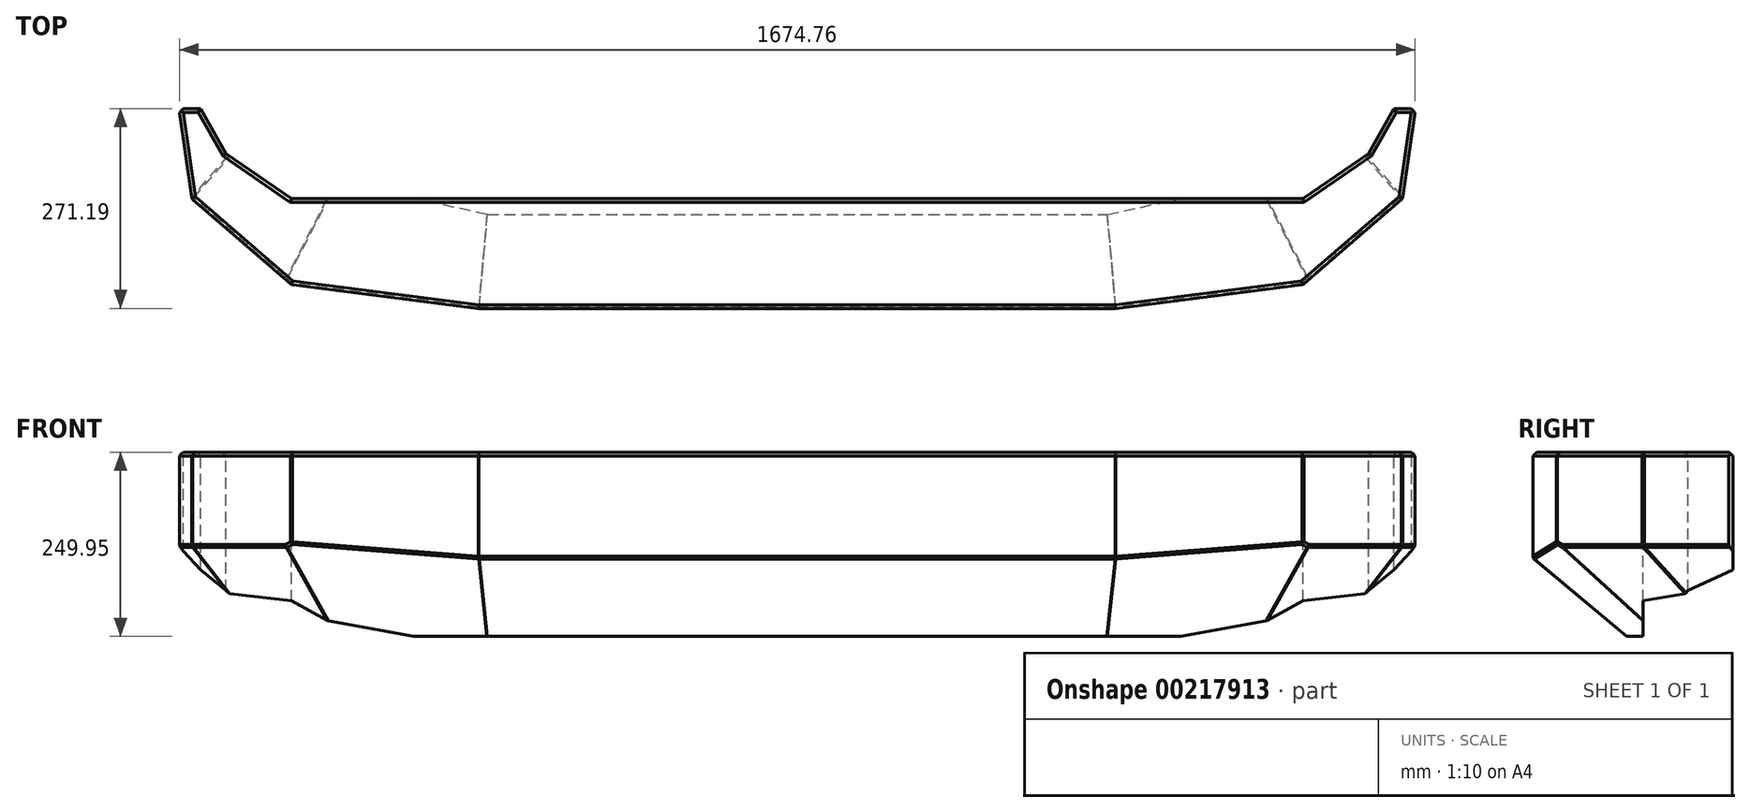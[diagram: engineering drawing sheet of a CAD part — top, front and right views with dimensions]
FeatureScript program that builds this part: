
annotation { "Feature Type Name" : "Feature", "Feature Type Description" : "" }
export const myFeature = defineFeature(function(context is Context, id is Id, definition is map)
    precondition{}
    {
        {
            var Q0;
            Q0=qCreatedBy(makeId("Top.planeOp"),FACE);
            var sketch = newSketch(context, id + "F0", { "sketchPlane" : qUnion([Q0])});
            skLineSegment(sketch, "E0", {"start": v(0, 0) * mm, "end": v(0, 79.38) * mm});
            skLineSegment(sketch, "E1", {"start": v(0, 0) * mm, "end": v(685.8, 0) * mm});
            skLineSegment(sketch, "E2", {"start": v(685.8, 0) * mm, "end": v(774.89, 60.96) * mm});
            skLineSegment(sketch, "E3", {"start": v(774.89, 60.96) * mm, "end": v(809, 121.92) * mm});
            skLineSegment(sketch, "E4", {"start": v(809, 121.92) * mm, "end": v(838.2, 121.92) * mm});
            skLineSegment(sketch, "E5", {"start": v(838.2, 121.92) * mm, "end": v(820.92, 0) * mm});
            skLineSegment(sketch, "E6", {"start": v(820.92, 0) * mm, "end": v(685.8, -117.08) * mm});
            skLineSegment(sketch, "E7", {"start": v(685.8, -117.08) * mm, "end": v(431.8, -149.27) * mm});
            skLineSegment(sketch, "E8", {"start": v(431.8, -149.27) * mm, "end": v(0, -149.27) * mm});
            skPoint(sketch, "E9", {"position": v(829.56, 60.96) * mm});
            skLineSegment(sketch, "E10.MirrorCS", {"start": v(0, 0) * mm, "end": v(-685.8, 0) * mm});
            skLineSegment(sketch, "E11.MirrorCS", {"start": v(-431.8, -149.27) * mm, "end": v(0, -149.27) * mm});
            skLineSegment(sketch, "E12.MirrorCS", {"start": v(-685.8, -117.08) * mm, "end": v(-431.8, -149.27) * mm});
            skLineSegment(sketch, "E13.MirrorCS", {"start": v(-820.92, 0) * mm, "end": v(-685.8, -117.08) * mm});
            skPoint(sketch, "E14.MirrorP", {"position": v(-829.56, 60.96) * mm});
            skLineSegment(sketch, "E15.MirrorCS", {"start": v(-838.2, 121.92) * mm, "end": v(-820.92, 0) * mm});
            skLineSegment(sketch, "E16.MirrorCS", {"start": v(-809, 121.92) * mm, "end": v(-838.2, 121.92) * mm});
            skLineSegment(sketch, "E17.MirrorCS", {"start": v(-774.89, 60.96) * mm, "end": v(-809, 121.92) * mm});
            skLineSegment(sketch, "E18.MirrorCS", {"start": v(-685.8, 0) * mm, "end": v(-774.89, 60.96) * mm});
            skSolve(sketch);
        }
        {
            var Q0;
            Q0 = qSketchRegion(id + "F0", true);
            extrude(context, id + "F1", {"entities" : qUnion([Q0]), "oppositeDirection" : true, "depth" : 254 * mm});
        }
        {
            var Q0;
            Q0=makeQuery(id+"F1.opExtrude","CAP_EDGE",EDGE,{"disambiguationData":[OSD([sQuery(id+"F0.wireOp",EDGE,"E8"),sQuery(id+"F0.wireOp",EDGE,"E11.MirrorCS")])],"isStart":true});
            cPlane(context, id + "F2", {"entities" : qUnion([Q0]), "cplaneType" : CPlaneType.LINE_ANGLE, "offset" : 25.4 * mm, "angle" : 320 * degree, "width" : 152.4 * mm, "height" : 152.4 * mm});
        }
        {
            var Q0;
            Q0=qCreatedBy(id+"F2.planeOp",FACE);
            var sketch = newSketch(context, id + "F3", { "sketchPlane" : qUnion([Q0])});
            skLineSegment(sketch, "E19", {"start": v(431.8, -205.66) * mm, "end": v(-431.8, -205.66) * mm});
            skLineSegment(sketch, "E20", {"start": v(-431.8, -205.66) * mm, "end": v(-431.8, -290.53) * mm});
            skLineSegment(sketch, "E21", {"start": v(-431.8, -290.53) * mm, "end": v(431.8, -290.53) * mm});
            skLineSegment(sketch, "E22", {"start": v(431.8, -290.53) * mm, "end": v(431.8, -205.66) * mm});
            skSolve(sketch);
        }
        {
            var Q0;
            Q0 = qSketchRegion(id + "F3", true);
            extrude(context, id + "F4", {"entities" : qUnion([Q0]), "operationType" : NewBodyOperationType.REMOVE, "depth" : 381 * mm});
        }
        {
            var Q0;
            Q0=makeQuery(id+"F1.opExtrude","CAP_EDGE",EDGE,{"disambiguationData":[OSD([sQuery(id+"F0.wireOp",EDGE,"E12.MirrorCS")])],"isStart":true});
            cPlane(context, id + "F5", {"entities" : qUnion([Q0]), "cplaneType" : CPlaneType.LINE_ANGLE, "offset" : 25.4 * mm, "angle" : 320 * degree, "width" : 152.4 * mm, "height" : 152.4 * mm});
        }
        {
            var Q0;
            Q0=qCreatedBy(id+"F5.planeOp",FACE);
            var sketch = newSketch(context, id + "F6", { "sketchPlane" : qUnion([Q0])});
            skLineSegment(sketch, "E23", {"start": v(427.72, -205.74) * mm, "end": v(689.8, -168.73) * mm});
            skLineSegment(sketch, "E24", {"start": v(689.8, -168.73) * mm, "end": v(689.8, -269.54) * mm});
            skLineSegment(sketch, "E25", {"start": v(689.8, -269.54) * mm, "end": v(434.61, -290.33) * mm});
            skLineSegment(sketch, "E26", {"start": v(434.61, -290.33) * mm, "end": v(427.72, -205.74) * mm});
            skSolve(sketch);
        }
        {
            var Q0;
            Q0=makeQuery(id+"F6.imprint","IMPRINT",FACE,{"disambiguationData":[TD([[makeQuery(id+"F6.imprint","IMPRINT",EDGE,{"derivedFrom":sQuery(id+"F6.wireOp",EDGE,"E23")}),-1.0]])]});
            extrude(context, id + "F7", {"entities" : qUnion([Q0]), "operationType" : NewBodyOperationType.REMOVE, "depth" : 381 * mm});
        }
        {
            var Q0;
            Q0=makeQuery(id+"F1.opExtrude","CAP_EDGE",EDGE,{"disambiguationData":[OSD([sQuery(id+"F0.wireOp",EDGE,"E13.MirrorCS")])],"isStart":true});
            cPlane(context, id + "F8", {"entities" : qUnion([Q0]), "cplaneType" : CPlaneType.LINE_ANGLE, "offset" : 25.4 * mm, "angle" : 320 * degree, "width" : 152.4 * mm, "height" : 152.4 * mm});
        }
        {
            var Q0;
            Q0=qCreatedBy(id+"F8.planeOp",FACE);
            var sketch = newSketch(context, id + "F9", { "sketchPlane" : qUnion([Q0])});
            skLineSegment(sketch, "E27", {"start": v(-610.05, 167.48) * mm, "end": v(-757.65, 85.27) * mm});
            skLineSegment(sketch, "E28", {"start": v(-757.65, 85.27) * mm, "end": v(-804.84, 169.99) * mm});
            skLineSegment(sketch, "E29", {"start": v(-804.84, 169.99) * mm, "end": v(-648.64, 256.98) * mm});
            skLineSegment(sketch, "E30", {"start": v(-648.64, 256.98) * mm, "end": v(-610.05, 167.48) * mm});
            skSolve(sketch);
        }
        {
            var Q0;
            Q0 = qSketchRegion(id + "F9", true);
            extrude(context, id + "F10", {"entities" : qUnion([Q0]), "operationType" : NewBodyOperationType.REMOVE, "depth" : 381 * mm});
        }
        {
            var Q0;
            Q0=makeQuery(id+"F1.opExtrude","CAP_EDGE",EDGE,{"disambiguationData":[OSD([sQuery(id+"F0.wireOp",EDGE,"E15.MirrorCS")])],"isStart":true});
            cPlane(context, id + "F11", {"entities" : qUnion([Q0]), "cplaneType" : CPlaneType.LINE_ANGLE, "offset" : 25.4 * mm, "angle" : 42 * degree, "width" : 152.4 * mm, "height" : 152.4 * mm});
        }
        {
            var Q0;
            Q0=qCreatedBy(id+"F11.planeOp",FACE);
            var sketch = newSketch(context, id + "F12", { "sketchPlane" : qUnion([Q0])});
            skLineSegment(sketch, "E31", {"start": v(-698.66, 15.97) * mm, "end": v(-721.72, -105) * mm});
            skLineSegment(sketch, "E32", {"start": v(-721.72, -105) * mm, "end": v(-804.93, -89.13) * mm});
            skLineSegment(sketch, "E33", {"start": v(-804.93, -89.13) * mm, "end": v(-781.87, 31.83) * mm});
            skLineSegment(sketch, "E34", {"start": v(-781.87, 31.83) * mm, "end": v(-698.66, 15.97) * mm});
            skSolve(sketch);
        }
        {
            var Q0;
            Q0 = qSketchRegion(id + "F12", true);
            extrude(context, id + "F13", {"entities" : qUnion([Q0]), "operationType" : NewBodyOperationType.REMOVE, "depth" : 381 * mm});
        }
        {
            var Q0;
            Q0=makeQuery(id+"F1.opExtrude","CAP_EDGE",EDGE,{"disambiguationData":[OSD([sQuery(id+"F0.wireOp",EDGE,"E7")])],"isStart":true});
            cPlane(context, id + "F14", {"entities" : qUnion([Q0]), "cplaneType" : CPlaneType.LINE_ANGLE, "offset" : 25.4 * mm, "angle" : 40 * degree, "width" : 152.4 * mm, "height" : 152.4 * mm});
        }
        {
            var Q0;
            Q0=qCreatedBy(id+"F14.planeOp",FACE);
            var sketch = newSketch(context, id + "F15", { "sketchPlane" : qUnion([Q0])});
            skLineSegment(sketch, "E35", {"start": v(427.72, -205.74) * mm, "end": v(689.8, -168.73) * mm});
            skLineSegment(sketch, "E36", {"start": v(689.8, -168.73) * mm, "end": v(689.8, -269.54) * mm});
            skLineSegment(sketch, "E37", {"start": v(689.8, -269.54) * mm, "end": v(434.61, -290.33) * mm});
            skLineSegment(sketch, "E38", {"start": v(434.61, -290.33) * mm, "end": v(427.72, -205.74) * mm});
            skSolve(sketch);
        }
        {
            var Q0;
            Q0 = qSketchRegion(id + "F15", true);
            extrude(context, id + "F16", {"entities" : qUnion([Q0]), "operationType" : NewBodyOperationType.REMOVE, "oppositeDirection" : true, "depth" : 381 * mm});
        }
        {
            var Q0;
            Q0=makeQuery(id+"F1.opExtrude","CAP_EDGE",EDGE,{"disambiguationData":[OSD([sQuery(id+"F0.wireOp",EDGE,"E6")])],"isStart":true});
            cPlane(context, id + "F17", {"entities" : qUnion([Q0]), "cplaneType" : CPlaneType.LINE_ANGLE, "offset" : 25.4 * mm, "angle" : 40 * degree, "width" : 152.4 * mm, "height" : 152.4 * mm});
        }
        {
            var Q0;
            Q0=qCreatedBy(id+"F17.planeOp",FACE);
            var sketch = newSketch(context, id + "F18", { "sketchPlane" : qUnion([Q0])});
            skLineSegment(sketch, "E39", {"start": v(610.05, -167.48) * mm, "end": v(757.65, -85.27) * mm});
            skLineSegment(sketch, "E40", {"start": v(757.65, -85.27) * mm, "end": v(804.84, -169.99) * mm});
            skLineSegment(sketch, "E41", {"start": v(804.84, -169.99) * mm, "end": v(648.64, -256.98) * mm});
            skLineSegment(sketch, "E42", {"start": v(648.64, -256.98) * mm, "end": v(610.05, -167.48) * mm});
            skSolve(sketch);
        }
        {
            var Q0;
            Q0 = qSketchRegion(id + "F18", true);
            extrude(context, id + "F19", {"entities" : qUnion([Q0]), "operationType" : NewBodyOperationType.REMOVE, "oppositeDirection" : true, "depth" : 381 * mm});
        }
        {
            var Q0;
            Q0=makeQuery(id+"F1.opExtrude","CAP_EDGE",EDGE,{"disambiguationData":[OSD([sQuery(id+"F0.wireOp",EDGE,"E5")])],"isStart":true});
            cPlane(context, id + "F20", {"entities" : qUnion([Q0]), "cplaneType" : CPlaneType.LINE_ANGLE, "offset" : 25.4 * mm, "angle" : 318 * degree, "width" : 152.4 * mm, "height" : 152.4 * mm});
        }
        {
            var Q0;
            Q0=qCreatedBy(id+"F20.planeOp",FACE);
            var sketch = newSketch(context, id + "F21", { "sketchPlane" : qUnion([Q0])});
            skLineSegment(sketch, "E43", {"start": v(698.66, 15.97) * mm, "end": v(721.72, -105) * mm});
            skLineSegment(sketch, "E44", {"start": v(721.72, -105) * mm, "end": v(804.93, -89.13) * mm});
            skLineSegment(sketch, "E45", {"start": v(804.93, -89.13) * mm, "end": v(781.87, 31.83) * mm});
            skLineSegment(sketch, "E46", {"start": v(781.87, 31.83) * mm, "end": v(698.66, 15.97) * mm});
            skSolve(sketch);
        }
        {
            var Q0;
            Q0 = qSketchRegion(id + "F21", true);
            extrude(context, id + "F22", {"entities" : qUnion([Q0]), "operationType" : NewBodyOperationType.REMOVE, "depth" : 381 * mm});
        }
        {
            var Q0;
            Q0=makeQuery(id+"F1.opExtrude","SWEPT_FACE",FACE,{"disambiguationData":[OSD([sQuery(id+"F0.wireOp",EDGE,"E8"),sQuery(id+"F0.wireOp",EDGE,"E11.MirrorCS")])]});
            var sketch = newSketch(context, id + "F23", { "sketchPlane" : qUnion([Q0])});
            skLineSegment(sketch, "E47", {"start": v(-576.56, -249.95) * mm, "end": v(0, -249.95) * mm});
            skLineSegment(sketch, "E48", {"start": v(0, -249.95) * mm, "end": v(0, -297.74) * mm});
            skLineSegment(sketch, "E49", {"start": v(0, -297.74) * mm, "end": v(-576.56, -297.74) * mm});
            skLineSegment(sketch, "E50", {"start": v(-576.56, -297.74) * mm, "end": v(-576.56, -249.95) * mm});
            skLineSegment(sketch, "E51.MirrorCS", {"start": v(0, -297.74) * mm, "end": v(576.56, -297.74) * mm});
            skLineSegment(sketch, "E52.MirrorCS", {"start": v(576.56, -249.95) * mm, "end": v(0, -249.95) * mm});
            skLineSegment(sketch, "E53.MirrorCS", {"start": v(576.56, -297.74) * mm, "end": v(576.56, -249.95) * mm});
            skSolve(sketch);
        }
        {
            var Q0;
            Q0 = qSketchRegion(id + "F23", true);
            extrude(context, id + "F24", {"entities" : qUnion([Q0]), "operationType" : NewBodyOperationType.REMOVE, "oppositeDirection" : true, "depth" : 254 * mm});
        }
        {
            var Q0;
            Q0 = qSketchRegion(id + "F23", true);
            extrude(context, id + "F25", {"entities" : qUnion([Q0]), "operationType" : NewBodyOperationType.REMOVE, "oppositeDirection" : true, "depth" : 25.4 * mm});
        }
        {
            var Q0;
            Q0=makeQuery(id+"F1.opExtrude","CAP_EDGE",EDGE,{"disambiguationData":[OSD([sQuery(id+"F0.wireOp",EDGE,"E8"),sQuery(id+"F0.wireOp",EDGE,"E11.MirrorCS")])],"isStart":true});
            var Q1;
            Q1=makeQuery(id+"F1.opExtrude","CAP_EDGE",EDGE,{"disambiguationData":[OSD([sQuery(id+"F0.wireOp",EDGE,"E7")])],"isStart":true});
            var Q2;
            Q2=makeQuery(id+"F1.opExtrude","CAP_EDGE",EDGE,{"disambiguationData":[OSD([sQuery(id+"F0.wireOp",EDGE,"E6")])],"isStart":true});
            var Q3;
            Q3=makeQuery(id+"F1.opExtrude","CAP_EDGE",EDGE,{"disambiguationData":[OSD([sQuery(id+"F0.wireOp",EDGE,"E5")])],"isStart":true});
            var Q4;
            Q4=makeQuery(id+"F1.opExtrude","CAP_EDGE",EDGE,{"disambiguationData":[OSD([sQuery(id+"F0.wireOp",EDGE,"E4")])],"isStart":true});
            var Q5;
            Q5=makeQuery(id+"F1.opExtrude","CAP_EDGE",EDGE,{"disambiguationData":[OSD([sQuery(id+"F0.wireOp",EDGE,"E3")])],"isStart":true});
            var Q6;
            Q6=makeQuery(id+"F1.opExtrude","CAP_EDGE",EDGE,{"disambiguationData":[OSD([sQuery(id+"F0.wireOp",EDGE,"E2")])],"isStart":true});
            var Q7;
            Q7=makeQuery(id+"F1.opExtrude","CAP_EDGE",EDGE,{"disambiguationData":[OSD([sQuery(id+"F0.wireOp",EDGE,"E1"),sQuery(id+"F0.wireOp",EDGE,"E10.MirrorCS")])],"isStart":true});
            var Q8;
            Q8=makeQuery(id+"F1.opExtrude","CAP_EDGE",EDGE,{"disambiguationData":[OSD([sQuery(id+"F0.wireOp",EDGE,"E12.MirrorCS")])],"isStart":true});
            var Q9;
            Q9=makeQuery(id+"F1.opExtrude","CAP_EDGE",EDGE,{"disambiguationData":[OSD([sQuery(id+"F0.wireOp",EDGE,"E13.MirrorCS")])],"isStart":true});
            var Q10;
            Q10=makeQuery(id+"F1.opExtrude","CAP_EDGE",EDGE,{"disambiguationData":[OSD([sQuery(id+"F0.wireOp",EDGE,"E15.MirrorCS")])],"isStart":true});
            var Q11;
            Q11=makeQuery(id+"F1.opExtrude","CAP_EDGE",EDGE,{"disambiguationData":[OSD([sQuery(id+"F0.wireOp",EDGE,"E18.MirrorCS")])],"isStart":true});
            var Q12;
            Q12=makeQuery(id+"F1.opExtrude","CAP_EDGE",EDGE,{"disambiguationData":[OSD([sQuery(id+"F0.wireOp",EDGE,"E16.MirrorCS")])],"isStart":true});
            var Q13;
            Q13=makeQuery(id+"F1.opExtrude","CAP_EDGE",EDGE,{"disambiguationData":[OSD([sQuery(id+"F0.wireOp",EDGE,"E17.MirrorCS")])],"isStart":true});
            var Q14;
            Q14=makeQuery(id+"F7.boolean.opBoolean","INTERSECT",EDGE,{"derivedFrom":[makeQuery(id+"F1.opExtrude","SWEPT_FACE",FACE,{"disambiguationData":[OSD([sQuery(id+"F0.wireOp",EDGE,"E12.MirrorCS")])]}),makeQuery(id+"F7.opExtrude","SWEPT_FACE",FACE,{"disambiguationData":[OSD([sQuery(id+"F6.wireOp",EDGE,"E23")])]})]});
            var Q15;
            Q15=makeQuery(id+"F4.boolean.opBoolean","INTERSECT",EDGE,{"derivedFrom":[makeQuery(id+"F1.opExtrude","SWEPT_FACE",FACE,{"disambiguationData":[OSD([sQuery(id+"F0.wireOp",EDGE,"E8"),sQuery(id+"F0.wireOp",EDGE,"E11.MirrorCS")])]}),makeQuery(id+"F4.opExtrude","SWEPT_FACE",FACE,{"disambiguationData":[OSD([sQuery(id+"F3.wireOp",EDGE,"E19")])]})]});
            var Q16;
            Q16=makeQuery(id+"F7.boolean.opBoolean","INTERSECT",EDGE,{"derivedFrom":[makeQuery(id+"F1.opExtrude","SWEPT_FACE",FACE,{"disambiguationData":[OSD([sQuery(id+"F0.wireOp",EDGE,"E13.MirrorCS")])]}),makeQuery(id+"F7.opExtrude","SWEPT_FACE",FACE,{"disambiguationData":[OSD([sQuery(id+"F6.wireOp",EDGE,"E23")])]})]});
            var Q17;
            Q17=makeQuery(id+"F10.boolean.opBoolean","INTERSECT",EDGE,{"derivedFrom":[makeQuery(id+"F1.opExtrude","SWEPT_FACE",FACE,{"disambiguationData":[OSD([sQuery(id+"F0.wireOp",EDGE,"E13.MirrorCS")])]}),makeQuery(id+"F10.opExtrude","SWEPT_FACE",FACE,{"disambiguationData":[OSD([sQuery(id+"F9.wireOp",EDGE,"E27")])]})]});
            var Q18;
            Q18=makeQuery(id+"F13.boolean.opBoolean","INTERSECT",EDGE,{"derivedFrom":[makeQuery(id+"F1.opExtrude","SWEPT_FACE",FACE,{"disambiguationData":[OSD([sQuery(id+"F0.wireOp",EDGE,"E15.MirrorCS")])]}),makeQuery(id+"F13.opExtrude","SWEPT_FACE",FACE,{"disambiguationData":[OSD([sQuery(id+"F12.wireOp",EDGE,"E31")])]})]});
            var Q19;
            Q19=makeQuery(id+"F16.boolean.opBoolean","INTERSECT",EDGE,{"derivedFrom":[makeQuery(id+"F1.opExtrude","SWEPT_FACE",FACE,{"disambiguationData":[OSD([sQuery(id+"F0.wireOp",EDGE,"E7")])]}),makeQuery(id+"F16.opExtrude","SWEPT_FACE",FACE,{"disambiguationData":[OSD([sQuery(id+"F15.wireOp",EDGE,"E35")])]})]});
            var Q20;
            Q20=makeQuery(id+"F16.boolean.opBoolean","INTERSECT",EDGE,{"derivedFrom":[makeQuery(id+"F1.opExtrude","SWEPT_FACE",FACE,{"disambiguationData":[OSD([sQuery(id+"F0.wireOp",EDGE,"E6")])]}),makeQuery(id+"F16.opExtrude","SWEPT_FACE",FACE,{"disambiguationData":[OSD([sQuery(id+"F15.wireOp",EDGE,"E35")])]})]});
            var Q21;
            Q21=makeQuery(id+"F19.boolean.opBoolean","INTERSECT",EDGE,{"derivedFrom":[makeQuery(id+"F1.opExtrude","SWEPT_FACE",FACE,{"disambiguationData":[OSD([sQuery(id+"F0.wireOp",EDGE,"E6")])]}),makeQuery(id+"F19.opExtrude","SWEPT_FACE",FACE,{"disambiguationData":[OSD([sQuery(id+"F18.wireOp",EDGE,"E39")])]})]});
            var Q22;
            Q22=makeQuery(id+"F22.boolean.opBoolean","INTERSECT",EDGE,{"derivedFrom":[makeQuery(id+"F1.opExtrude","SWEPT_FACE",FACE,{"disambiguationData":[OSD([sQuery(id+"F0.wireOp",EDGE,"E5")])]}),makeQuery(id+"F22.opExtrude","SWEPT_FACE",FACE,{"disambiguationData":[OSD([sQuery(id+"F21.wireOp",EDGE,"E43")])]})]});
            chamfer(context, id + "F26", {"entities" : qUnion([Q0, Q1, Q2, Q3, Q4, Q5, Q6, Q7, Q8, Q9, Q10, Q11, Q12, Q13, Q14, Q15, Q16, Q17, Q18, Q19, Q20, Q21, Q22]), "width" : 5.08 * mm, "tangentPropagation" : true});
        }
        {
            var Q0;
            {var subQ0=sQuery(id+"F0.wireOp",EDGE,"E15.MirrorCS");var subQ1=sQuery(id+"F0.wireOp",EDGE,"E13.MirrorCS");Q0=makeQuery(id+"F10.boolean.opBoolean","SPLIT",EDGE,{"disambiguationData":[TD([makeQuery(id+"F1.opExtrude","CAP_FACE",FACE,{"disambiguationData":[OSD([sQuery(id+"F0.wireOp",EDGE,"E1"),sQuery(id+"F0.wireOp",EDGE,"E2"),sQuery(id+"F0.wireOp",EDGE,"E3"),sQuery(id+"F0.wireOp",EDGE,"E4"),sQuery(id+"F0.wireOp",EDGE,"E5"),sQuery(id+"F0.wireOp",EDGE,"E6"),sQuery(id+"F0.wireOp",EDGE,"E7"),sQuery(id+"F0.wireOp",EDGE,"E8"),sQuery(id+"F0.wireOp",EDGE,"E10.MirrorCS"),sQuery(id+"F0.wireOp",EDGE,"E11.MirrorCS"),sQuery(id+"F0.wireOp",EDGE,"E12.MirrorCS"),subQ1,subQ0,sQuery(id+"F0.wireOp",EDGE,"E16.MirrorCS"),sQuery(id+"F0.wireOp",EDGE,"E17.MirrorCS"),sQuery(id+"F0.wireOp",EDGE,"E18.MirrorCS")])],"isStart":true})])],"derivedFrom":makeQuery(id+"F1.opExtrude","SWEPT_EDGE",EDGE,{"disambiguationData":[OSD([subQ1,subQ0])]})});}
            var Q1;
            Q1=makeQuery(id+"F1.opExtrude","SWEPT_EDGE",EDGE,{"disambiguationData":[OSD([sQuery(id+"F0.wireOp",EDGE,"E12.MirrorCS"),sQuery(id+"F0.wireOp",EDGE,"E13.MirrorCS")])]});
            var Q2;
            Q2=makeQuery(id+"F1.opExtrude","SWEPT_EDGE",EDGE,{"disambiguationData":[OSD([sQuery(id+"F0.wireOp",EDGE,"E15.MirrorCS"),sQuery(id+"F0.wireOp",EDGE,"E16.MirrorCS")])]});
            var Q3;
            Q3=makeQuery(id+"F13.boolean.opBoolean","INTERSECT",EDGE,{"derivedFrom":[makeQuery(id+"F10.boolean.opBoolean","COPY",FACE,{"derivedFrom":makeQuery(id+"F10.opExtrude","SWEPT_FACE",FACE,{"disambiguationData":[OSD([sQuery(id+"F9.wireOp",EDGE,"E27")])]})}),makeQuery(id+"F13.opExtrude","SWEPT_FACE",FACE,{"disambiguationData":[OSD([sQuery(id+"F12.wireOp",EDGE,"E31")])]})]});
            var Q4;
            Q4=makeQuery(id+"F10.boolean.opBoolean","INTERSECT",EDGE,{"derivedFrom":[makeQuery(id+"F7.boolean.opBoolean","COPY",FACE,{"derivedFrom":makeQuery(id+"F7.opExtrude","SWEPT_FACE",FACE,{"disambiguationData":[OSD([sQuery(id+"F6.wireOp",EDGE,"E23")])]})}),makeQuery(id+"F10.opExtrude","SWEPT_FACE",FACE,{"disambiguationData":[OSD([sQuery(id+"F9.wireOp",EDGE,"E27")])]})]});
            var Q5;
            Q5=makeQuery(id+"F7.boolean.opBoolean","INTERSECT",EDGE,{"derivedFrom":[makeQuery(id+"F4.boolean.opBoolean","COPY",FACE,{"derivedFrom":makeQuery(id+"F4.opExtrude","SWEPT_FACE",FACE,{"disambiguationData":[OSD([sQuery(id+"F3.wireOp",EDGE,"E19")])]})}),makeQuery(id+"F7.opExtrude","SWEPT_FACE",FACE,{"disambiguationData":[OSD([sQuery(id+"F6.wireOp",EDGE,"E23")])]})]});
            var Q6;
            {var subQ0=sQuery(id+"F0.wireOp",EDGE,"E12.MirrorCS");var subQ1=sQuery(id+"F0.wireOp",EDGE,"E11.MirrorCS");var subQ2=sQuery(id+"F0.wireOp",EDGE,"E8");Q6=makeQuery(id+"F4.boolean.opBoolean","SPLIT",EDGE,{"disambiguationData":[TD([makeQuery(id+"F1.opExtrude","CAP_FACE",FACE,{"disambiguationData":[OSD([sQuery(id+"F0.wireOp",EDGE,"E1"),sQuery(id+"F0.wireOp",EDGE,"E2"),sQuery(id+"F0.wireOp",EDGE,"E3"),sQuery(id+"F0.wireOp",EDGE,"E4"),sQuery(id+"F0.wireOp",EDGE,"E5"),sQuery(id+"F0.wireOp",EDGE,"E6"),sQuery(id+"F0.wireOp",EDGE,"E7"),subQ2,sQuery(id+"F0.wireOp",EDGE,"E10.MirrorCS"),subQ1,subQ0,sQuery(id+"F0.wireOp",EDGE,"E13.MirrorCS"),sQuery(id+"F0.wireOp",EDGE,"E15.MirrorCS"),sQuery(id+"F0.wireOp",EDGE,"E16.MirrorCS"),sQuery(id+"F0.wireOp",EDGE,"E17.MirrorCS"),sQuery(id+"F0.wireOp",EDGE,"E18.MirrorCS")])],"isStart":true})])],"derivedFrom":makeQuery(id+"F1.opExtrude","SWEPT_EDGE",EDGE,{"disambiguationData":[OSD([subQ1,subQ0])]})});}
            var Q7;
            {var subQ0=sQuery(id+"F0.wireOp",EDGE,"E11.MirrorCS");var subQ1=sQuery(id+"F0.wireOp",EDGE,"E8");var subQ2=sQuery(id+"F0.wireOp",EDGE,"E7");Q7=makeQuery(id+"F4.boolean.opBoolean","SPLIT",EDGE,{"disambiguationData":[TD([makeQuery(id+"F1.opExtrude","CAP_FACE",FACE,{"disambiguationData":[OSD([sQuery(id+"F0.wireOp",EDGE,"E1"),sQuery(id+"F0.wireOp",EDGE,"E2"),sQuery(id+"F0.wireOp",EDGE,"E3"),sQuery(id+"F0.wireOp",EDGE,"E4"),sQuery(id+"F0.wireOp",EDGE,"E5"),sQuery(id+"F0.wireOp",EDGE,"E6"),subQ2,subQ1,sQuery(id+"F0.wireOp",EDGE,"E10.MirrorCS"),subQ0,sQuery(id+"F0.wireOp",EDGE,"E12.MirrorCS"),sQuery(id+"F0.wireOp",EDGE,"E13.MirrorCS"),sQuery(id+"F0.wireOp",EDGE,"E15.MirrorCS"),sQuery(id+"F0.wireOp",EDGE,"E16.MirrorCS"),sQuery(id+"F0.wireOp",EDGE,"E17.MirrorCS"),sQuery(id+"F0.wireOp",EDGE,"E18.MirrorCS")])],"isStart":true})])],"derivedFrom":makeQuery(id+"F1.opExtrude","SWEPT_EDGE",EDGE,{"disambiguationData":[OSD([subQ2,subQ1])]})});}
            var Q8;
            Q8=makeQuery(id+"F16.boolean.opBoolean","INTERSECT",EDGE,{"derivedFrom":[makeQuery(id+"F4.boolean.opBoolean","COPY",FACE,{"derivedFrom":makeQuery(id+"F4.opExtrude","SWEPT_FACE",FACE,{"disambiguationData":[OSD([sQuery(id+"F3.wireOp",EDGE,"E19")])]})}),makeQuery(id+"F16.opExtrude","SWEPT_FACE",FACE,{"disambiguationData":[OSD([sQuery(id+"F15.wireOp",EDGE,"E35")])]})]});
            var Q9;
            Q9=makeQuery(id+"F1.opExtrude","SWEPT_EDGE",EDGE,{"disambiguationData":[OSD([sQuery(id+"F0.wireOp",EDGE,"E6"),sQuery(id+"F0.wireOp",EDGE,"E7")])]});
            var Q10;
            Q10=makeQuery(id+"F19.boolean.opBoolean","INTERSECT",EDGE,{"derivedFrom":[makeQuery(id+"F16.boolean.opBoolean","COPY",FACE,{"derivedFrom":makeQuery(id+"F16.opExtrude","SWEPT_FACE",FACE,{"disambiguationData":[OSD([sQuery(id+"F15.wireOp",EDGE,"E35")])]})}),makeQuery(id+"F19.opExtrude","SWEPT_FACE",FACE,{"disambiguationData":[OSD([sQuery(id+"F18.wireOp",EDGE,"E39")])]})]});
            var Q11;
            {var subQ0=sQuery(id+"F0.wireOp",EDGE,"E6");var subQ1=sQuery(id+"F0.wireOp",EDGE,"E5");Q11=makeQuery(id+"F19.boolean.opBoolean","SPLIT",EDGE,{"disambiguationData":[TD([makeQuery(id+"F1.opExtrude","CAP_FACE",FACE,{"disambiguationData":[OSD([sQuery(id+"F0.wireOp",EDGE,"E1"),sQuery(id+"F0.wireOp",EDGE,"E2"),sQuery(id+"F0.wireOp",EDGE,"E3"),sQuery(id+"F0.wireOp",EDGE,"E4"),subQ1,subQ0,sQuery(id+"F0.wireOp",EDGE,"E7"),sQuery(id+"F0.wireOp",EDGE,"E8"),sQuery(id+"F0.wireOp",EDGE,"E10.MirrorCS"),sQuery(id+"F0.wireOp",EDGE,"E11.MirrorCS"),sQuery(id+"F0.wireOp",EDGE,"E12.MirrorCS"),sQuery(id+"F0.wireOp",EDGE,"E13.MirrorCS"),sQuery(id+"F0.wireOp",EDGE,"E15.MirrorCS"),sQuery(id+"F0.wireOp",EDGE,"E16.MirrorCS"),sQuery(id+"F0.wireOp",EDGE,"E17.MirrorCS"),sQuery(id+"F0.wireOp",EDGE,"E18.MirrorCS")])],"isStart":true})])],"derivedFrom":makeQuery(id+"F1.opExtrude","SWEPT_EDGE",EDGE,{"disambiguationData":[OSD([subQ1,subQ0])]})});}
            var Q12;
            Q12=makeQuery(id+"F22.boolean.opBoolean","INTERSECT",EDGE,{"derivedFrom":[makeQuery(id+"F19.boolean.opBoolean","COPY",FACE,{"derivedFrom":makeQuery(id+"F19.opExtrude","SWEPT_FACE",FACE,{"disambiguationData":[OSD([sQuery(id+"F18.wireOp",EDGE,"E39")])]})}),makeQuery(id+"F22.opExtrude","SWEPT_FACE",FACE,{"disambiguationData":[OSD([sQuery(id+"F21.wireOp",EDGE,"E43")])]})]});
            var Q13;
            Q13=makeQuery(id+"F1.opExtrude","SWEPT_EDGE",EDGE,{"disambiguationData":[OSD([sQuery(id+"F0.wireOp",EDGE,"E4"),sQuery(id+"F0.wireOp",EDGE,"E5")])]});
            chamfer(context, id + "F27", {"entities" : qUnion([Q0, Q1, Q2, Q3, Q4, Q5, Q6, Q7, Q8, Q9, Q10, Q11, Q12, Q13]), "width" : 5.08 * mm, "tangentPropagation" : true});
        }
    });
